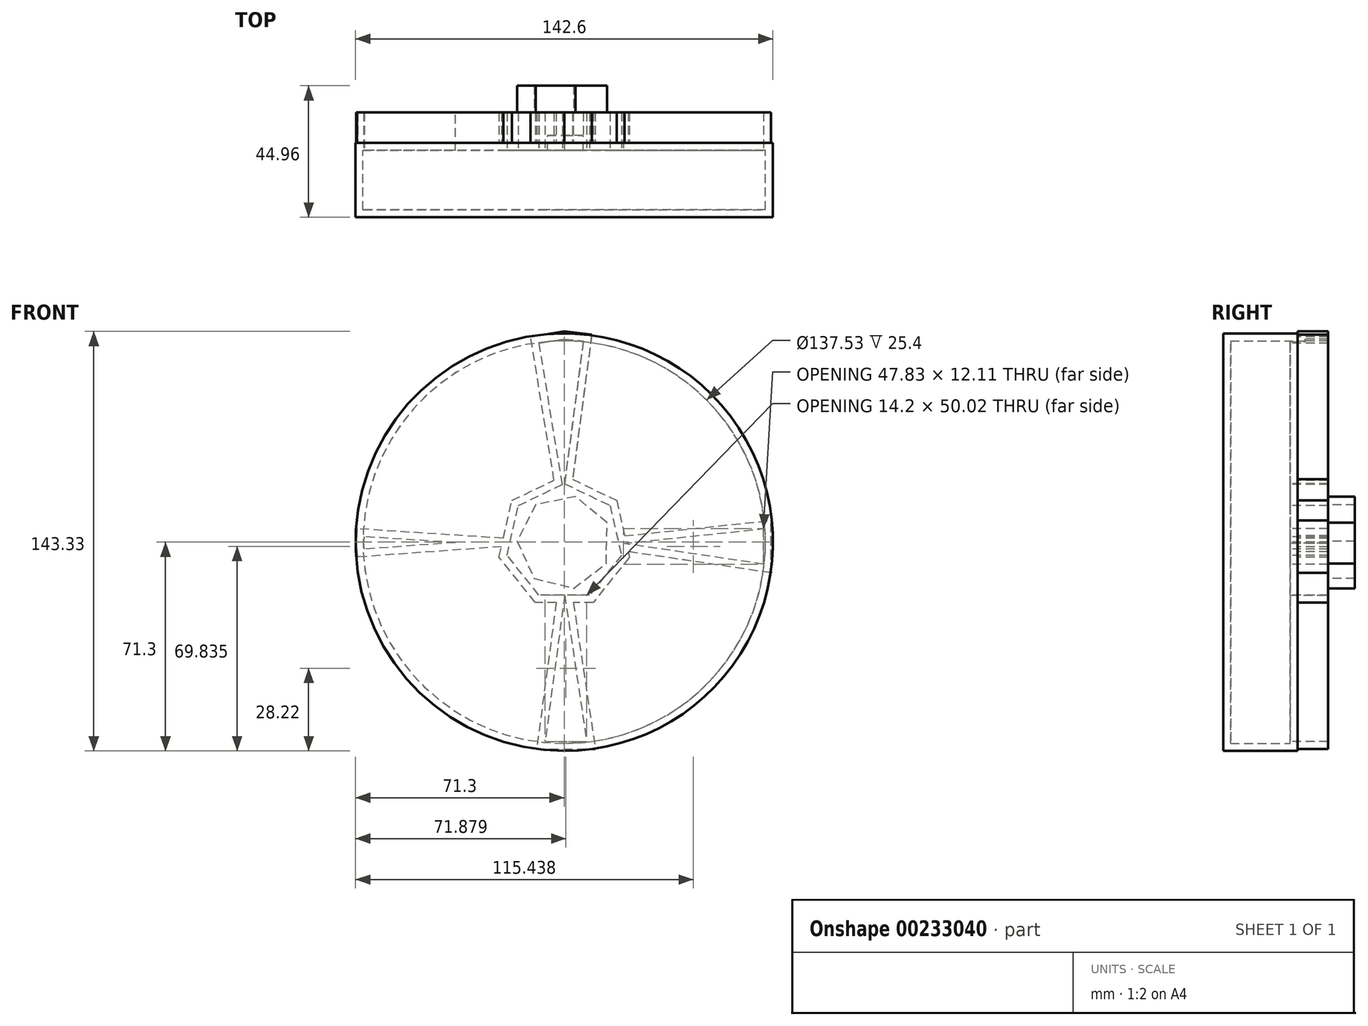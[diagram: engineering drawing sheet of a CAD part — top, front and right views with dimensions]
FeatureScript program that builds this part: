
annotation { "Feature Type Name" : "Feature", "Feature Type Description" : "" }
export const myFeature = defineFeature(function(context is Context, id is Id, definition is map)
    precondition{}
    {
        {
            var Q0;
            Q0=qCreatedBy(makeId("Front.planeOp"),FACE);
            var sketch = newSketch(context, id + "F0", { "sketchPlane" : qUnion([Q0])});
            skCircle(sketch, "E0", {"center": v(0, 0) * mm, "radius": 71.3 * mm});
            skSolve(sketch);
        }
        {
            var Q0;
            Q0=makeQuery(id+"F0.imprint","IMPRINT",FACE,{"disambiguationData":[TD([[makeQuery(id+"F0.imprint","IMPRINT",EDGE,{"derivedFrom":sQuery(id+"F0.wireOp",EDGE,"E0")}),1.0]])]});
            var sketch = newSketch(context, id + "F1", { "sketchPlane" : qUnion([Q0])});
            skLineSegment(sketch, "E1", {"start": v(0, 72.03) * mm, "end": v(0, 0) * mm});
            skLineSegment(sketch, "E2", {"start": v(9.4, 71) * mm, "end": v(0, 0) * mm});
            skLineSegment(sketch, "E3", {"start": v(0, 0) * mm, "end": v(-11.5, 70.16) * mm});
            skLineSegment(sketch, "E4", {"start": v(0, 0) * mm, "end": v(10.63, -70.63) * mm});
            skLineSegment(sketch, "E5", {"start": v(0, 0) * mm, "end": v(0, -70.63) * mm});
            skLineSegment(sketch, "E6", {"start": v(0, 0) * mm, "end": v(-9.42, -70.63) * mm});
            skCircle(sketch, "E7.cCircle", {"center": v(0, 0) * mm, "radius": 20.6 * mm, "construction": true});
            skLineSegment(sketch, "E7.0", {"start": v(9.92, -20.6) * mm, "end": v(-9.92, -20.6) * mm});
            skLineSegment(sketch, "E7.1", {"start": v(-9.92, -20.6) * mm, "end": v(-22.29, -5.09) * mm});
            skLineSegment(sketch, "E7.2", {"start": v(-22.29, -5.09) * mm, "end": v(-17.87, 14.25) * mm});
            skLineSegment(sketch, "E7.3", {"start": v(-17.87, 14.25) * mm, "end": v(0, 22.86) * mm});
            skLineSegment(sketch, "E7.4", {"start": v(0, 22.86) * mm, "end": v(17.87, 14.25) * mm});
            skLineSegment(sketch, "E7.5", {"start": v(17.87, 14.25) * mm, "end": v(22.29, -5.09) * mm});
            skLineSegment(sketch, "E7.6", {"start": v(22.29, -5.09) * mm, "end": v(9.92, -20.6) * mm});
            skPoint(sketch, "E7.0.midPoint", {"position": v(0, -20.6) * mm});
            skLineSegment(sketch, "E8", {"start": v(70.6, 0) * mm, "end": v(0, 0) * mm});
            skLineSegment(sketch, "E9", {"start": v(70.59, -10.47) * mm, "end": v(0, 0) * mm});
            skLineSegment(sketch, "E10", {"start": v(0, 0) * mm, "end": v(70.6, 7.41) * mm});
            skLineSegment(sketch, "E11", {"start": v(0, 0) * mm, "end": v(-70.62, -5.09) * mm});
            skLineSegment(sketch, "E12", {"start": v(0, 0) * mm, "end": v(-71.03, 0) * mm});
            skLineSegment(sketch, "E13", {"start": v(0, 0) * mm, "end": v(-70.83, 4.58) * mm});
            skPoint(sketch, "E13.endSnap0", {"position": v(-20.08, 4.58) * mm});
            skLineSegment(sketch, "E14", {"start": v(-11.5, 70.16) * mm, "end": v(0, 72.03) * mm});
            skLineSegment(sketch, "E15", {"start": v(0, 72.03) * mm, "end": v(9.4, 71) * mm});
            skLineSegment(sketch, "E16", {"start": v(-9.42, -70.63) * mm, "end": v(0, -70.63) * mm});
            skLineSegment(sketch, "E17", {"start": v(0, -70.63) * mm, "end": v(10.63, -70.63) * mm});
            skLineSegment(sketch, "E18", {"start": v(-70.83, 4.58) * mm, "end": v(-71.03, 0) * mm});
            skLineSegment(sketch, "E19", {"start": v(-70.62, -5.09) * mm, "end": v(-71.03, 0) * mm});
            skLineSegment(sketch, "E20", {"start": v(70.59, -10.47) * mm, "end": v(70.6, 0) * mm});
            skLineSegment(sketch, "E21", {"start": v(70.6, 0) * mm, "end": v(70.6, 7.41) * mm});
            skSolve(sketch);
        }
        {
            var Q0;
            Q0 = qSketchRegion(id + "F0", true);
            extrude(context, id + "F2", {"entities" : qUnion([Q0]), "depth" : 25.4 * mm});
        }
        {
            var Q0;
            Q0 = qSketchRegion(id + "F1", true);
            extrude(context, id + "F3", {"entities" : qUnion([Q0]), "operationType" : NewBodyOperationType.ADD, "oppositeDirection" : true, "depth" : 10.4 * mm});
        }
        {
            var Q0;
            Q0=makeQuery(id+"F3.opExtrude","CAP_FACE",FACE,{"disambiguationData":[OSD([sQuery(id+"F1.wireOp",EDGE,"E2"),sQuery(id+"F1.wireOp",EDGE,"E3"),sQuery(id+"F1.wireOp",EDGE,"E4"),sQuery(id+"F1.wireOp",EDGE,"E6"),sQuery(id+"F1.wireOp",EDGE,"E7.0"),sQuery(id+"F1.wireOp",EDGE,"E7.1"),sQuery(id+"F1.wireOp",EDGE,"E7.2"),sQuery(id+"F1.wireOp",EDGE,"E7.3"),sQuery(id+"F1.wireOp",EDGE,"E7.4"),sQuery(id+"F1.wireOp",EDGE,"E7.5"),sQuery(id+"F1.wireOp",EDGE,"E7.6"),sQuery(id+"F1.wireOp",EDGE,"E9"),sQuery(id+"F1.wireOp",EDGE,"E10"),sQuery(id+"F1.wireOp",EDGE,"E11"),sQuery(id+"F1.wireOp",EDGE,"E13"),sQuery(id+"F1.wireOp",EDGE,"E14"),sQuery(id+"F1.wireOp",EDGE,"E15"),sQuery(id+"F1.wireOp",EDGE,"E16"),sQuery(id+"F1.wireOp",EDGE,"E17"),sQuery(id+"F1.wireOp",EDGE,"E18"),sQuery(id+"F1.wireOp",EDGE,"E19"),sQuery(id+"F1.wireOp",EDGE,"E20"),sQuery(id+"F1.wireOp",EDGE,"E21")])],"isStart":false});
            shell(context, id + "F4", {"entities" : qUnion([Q0]), "thickness" : 2.54 * mm});
        }
        {
            var Q0;
            Q0=makeQuery(id+"F3.opExtrude","CAP_FACE",FACE,{"disambiguationData":[OSD([sQuery(id+"F1.wireOp",EDGE,"E2"),sQuery(id+"F1.wireOp",EDGE,"E3"),sQuery(id+"F1.wireOp",EDGE,"E4"),sQuery(id+"F1.wireOp",EDGE,"E6"),sQuery(id+"F1.wireOp",EDGE,"E7.0"),sQuery(id+"F1.wireOp",EDGE,"E7.1"),sQuery(id+"F1.wireOp",EDGE,"E7.2"),sQuery(id+"F1.wireOp",EDGE,"E7.3"),sQuery(id+"F1.wireOp",EDGE,"E7.4"),sQuery(id+"F1.wireOp",EDGE,"E7.5"),sQuery(id+"F1.wireOp",EDGE,"E7.6"),sQuery(id+"F1.wireOp",EDGE,"E9"),sQuery(id+"F1.wireOp",EDGE,"E10"),sQuery(id+"F1.wireOp",EDGE,"E11"),sQuery(id+"F1.wireOp",EDGE,"E13"),sQuery(id+"F1.wireOp",EDGE,"E14"),sQuery(id+"F1.wireOp",EDGE,"E15"),sQuery(id+"F1.wireOp",EDGE,"E16"),sQuery(id+"F1.wireOp",EDGE,"E17"),sQuery(id+"F1.wireOp",EDGE,"E18"),sQuery(id+"F1.wireOp",EDGE,"E19"),sQuery(id+"F1.wireOp",EDGE,"E20"),sQuery(id+"F1.wireOp",EDGE,"E21")])],"isStart":false});
            var sketch = newSketch(context, id + "F5", { "sketchPlane" : qUnion([Q0])});
            skCircle(sketch, "E22.cCircle", {"center": v(0, 0) * mm, "radius": 14.5 * mm, "construction": true});
            skLineSegment(sketch, "E22.0", {"start": v(10.28, -12.37) * mm, "end": v(-3.26, -15.75) * mm});
            skLineSegment(sketch, "E22.1", {"start": v(-3.26, -15.75) * mm, "end": v(-14.34, -7.28) * mm});
            skLineSegment(sketch, "E22.2", {"start": v(-14.34, -7.28) * mm, "end": v(-14.63, 6.68) * mm});
            skLineSegment(sketch, "E22.3", {"start": v(-14.63, 6.68) * mm, "end": v(-3.9, 15.6) * mm});
            skLineSegment(sketch, "E22.4", {"start": v(-3.9, 15.6) * mm, "end": v(9.77, 12.78) * mm});
            skLineSegment(sketch, "E22.5", {"start": v(9.77, 12.78) * mm, "end": v(16.08, 0.33) * mm});
            skLineSegment(sketch, "E22.6", {"start": v(16.08, 0.33) * mm, "end": v(10.28, -12.37) * mm});
            skPoint(sketch, "E22.0.midPoint", {"position": v(3.51, -14.06) * mm});
            skSolve(sketch);
        }
        {
            var Q0;
            Q0=makeQuery(id+"F5.imprint","IMPRINT",FACE,{"disambiguationData":[TD([[makeQuery(id+"F5.imprint","IMPRINT",EDGE,{"derivedFrom":sQuery(id+"F5.wireOp",EDGE,"E22.0")}),-1.0]])]});
            extrude(context, id + "F6", {"entities" : qUnion([Q0]), "depth" : 9.14 * mm});
        }
    });
